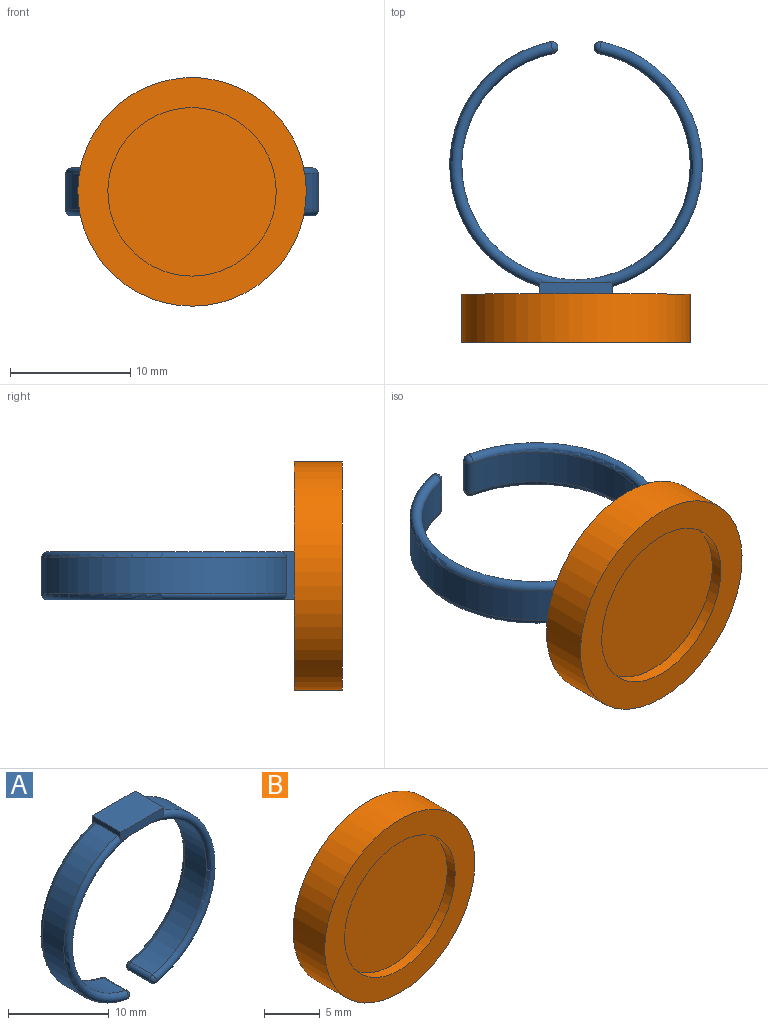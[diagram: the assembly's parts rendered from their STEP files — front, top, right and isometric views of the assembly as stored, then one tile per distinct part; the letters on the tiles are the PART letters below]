
ASSEMBLY  parts=2 mates=1
PART A: 22 faces, bbox 22.8x4.1x22.5 mm
  f0: cylinder r=10.5mm len=20.35mm, axis (0,1,0), area 83.5mm2, adj f1,f2,f5,f19
  f1: torus R=10mm, axis (0,-1,0), area 86.6mm2, adj f0,f4,f6,f7,f8,f12,f13,f14
  f2: torus R=10mm, axis (0,-1,0), area 86.6mm2, adj f0,f4,f6,f9,f10,f15,f16,f18
  f3: cylinder r=0.5mm len=3mm, axis (0,1,0), area 4.7mm2, adj f4,f6,f8,f10
  f4: cylinder r=9.5mm len=19mm, axis (0,1,0), area 167.6mm2, adj f1,f2,f3,f5
  f5: cylinder r=0.5mm len=3mm, axis (0,1,0), area 4.7mm2, adj f0,f4,f7,f9
  f6: cylinder r=10.5mm len=20.35mm, axis (0,1,0), area 83.5mm2, adj f1,f2,f3,f21
  f7: sphere r=0.5mm, area 0.8mm2, adj f1,f5
  f8: sphere r=0.5mm, area 0.8mm2, adj f1,f3
  f9: sphere r=0.5mm, area 0.8mm2, adj f2,f5
  f10: sphere r=0.5mm, area 0.8mm2, adj f2,f3
  f11: plane 6x1mm, normal (0,1,0), area 6mm2, adj f12,f13,f14,f19,f20,f21
  f12: plane 0.58x0.04mm, normal (0,0,-1), area 0mm2, adj f1,f11,f21
  f13: plane 0.58x0.04mm, normal (0,0,-1), area 0mm2, adj f1,f11,f19
  f14: plane 4.86x0.1mm, normal (0,0,-1), area 0.3mm2, adj f1,f11
  f15: plane 0.58x0.04mm, normal (0,0,-1), area 0mm2, adj f2,f17,f19
  f16: plane 0.58x0.04mm, normal (0,0,-1), area 0mm2, adj f2,f17,f21
  f17: plane 6x1mm, normal (0,-1,0), area 6mm2, adj f15,f16,f18,f19,f20,f21
  f18: plane 4.86x0.1mm, normal (0,0,-1), area 0.3mm2, adj f2,f17
  f19: plane 4.05x1.05mm, normal (1,0,0), area 2.7mm2, adj f0,f1,f2,f11,f13,f15,f17,f20
  f20: plane 6x4mm, normal (0,0,1), area 24mm2, adj f11,f17,f19,f21
  f21: plane 4.05x1.05mm, normal (-1,0,0), area 2.7mm2, adj f1,f2,f6,f11,f12,f16,f17,f20
PART B: 10 faces, bbox 19x4x19 mm
  f0: plane 19x19mm, normal (0,1,0), area 254.3mm2, adj f2,f5,f6,f7,f8
  f1: cylinder r=7mm len=14mm, axis (0,1,0), area 44mm2, adj f3,f4
  f2: cylinder r=9.5mm len=19mm, axis (0,1,0), area 238.8mm2, adj f0,f3
  f3: plane 19x19mm, normal (0,-1,0), area 129.6mm2, adj f1,f2
  f4: plane 14x14mm, normal (0,-1,0), area 153.9mm2, adj f1
  f5: plane 6.5x1mm, normal (0,0,-1), area 6.5mm2, adj f0,f6,f8,f9
  f6: plane 4.5x1mm, normal (-1,0,0), area 4.5mm2, adj f0,f5,f7,f9
  f7: plane 6.5x1mm, normal (0,0,1), area 6.5mm2, adj f0,f6,f8,f9
  f8: plane 4.5x1mm, normal (1,0,0), area 4.5mm2, adj f0,f5,f7,f9
  f9: plane 6.5x4.5mm, normal (0,1,0), area 29.2mm2, adj f5,f6,f7,f8
PLACE A rot(axis=(1,0,0),90deg) t=(23.32,40.83,-7.71)mm
PLACE B t=(-22.08,-7.5,-9.71)mm
MATE parallel B.f2 <-> A.f20  axis (0,1,0) through (-22.08,-7.5,-9.71)mm
